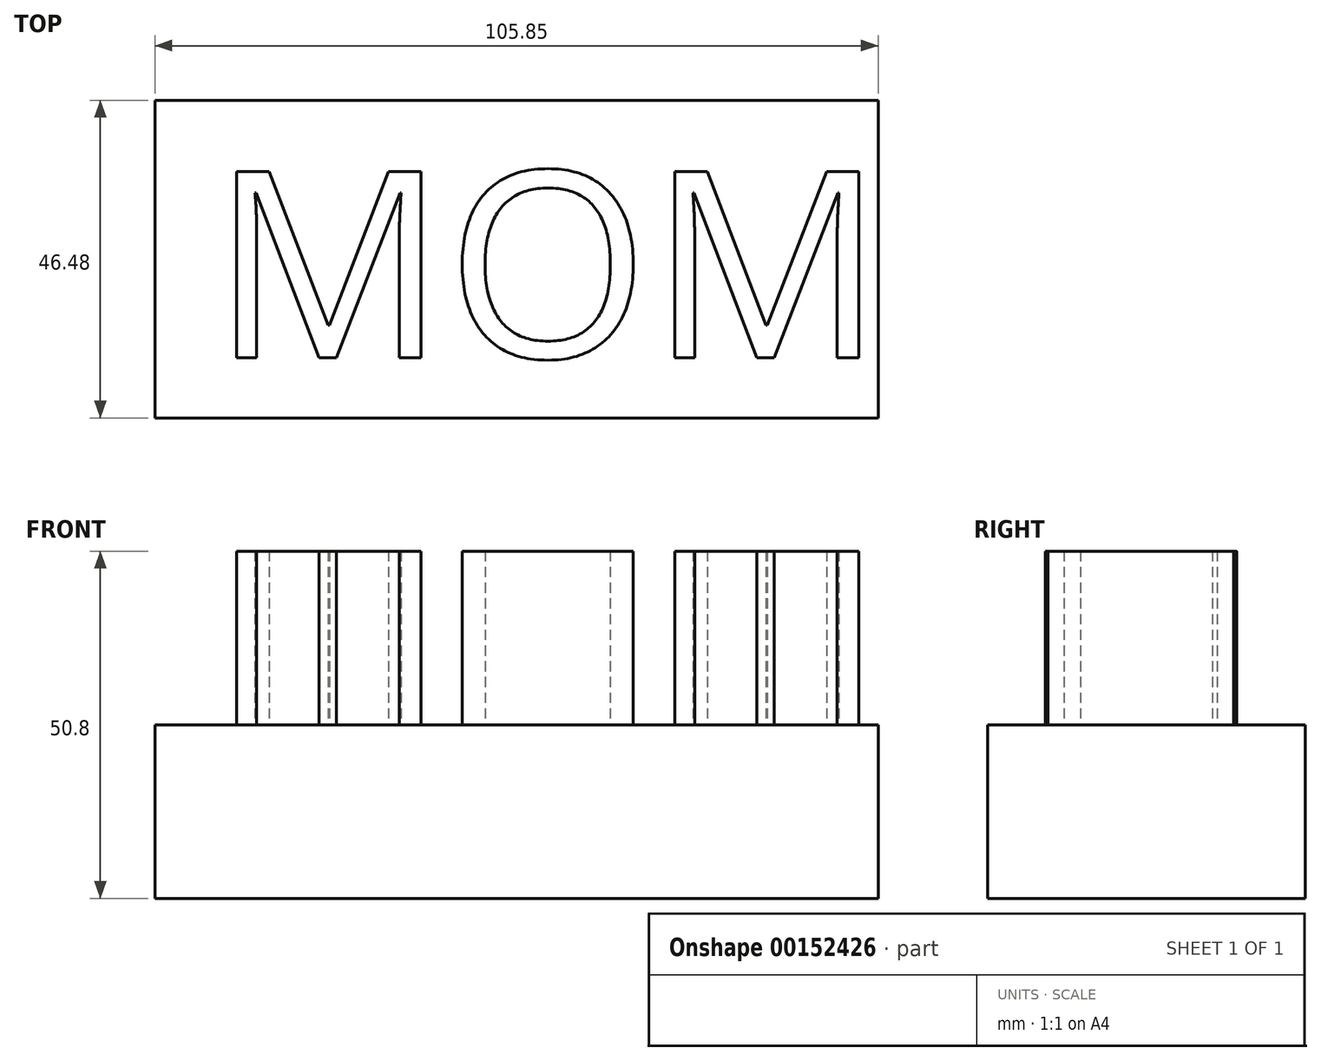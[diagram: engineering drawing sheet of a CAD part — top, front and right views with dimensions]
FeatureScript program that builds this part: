
annotation { "Feature Type Name" : "Feature", "Feature Type Description" : "" }
export const myFeature = defineFeature(function(context is Context, id is Id, definition is map)
    precondition{}
    {
        {
            var Q0;
            Q0=qCreatedBy(makeId("Top.planeOp"),FACE);
            var sketch = newSketch(context, id + "F0", { "sketchPlane" : qUnion([Q0])});
            skLineSegment(sketch, "E0.bottom", {"start": v(-45.3, 42.76) * mm, "end": v(35.16, 42.76) * mm});
            skLineSegment(sketch, "E0.top", {"start": v(-45.3, -3.72) * mm, "end": v(35.16, -3.72) * mm});
            skLineSegment(sketch, "E0.left", {"start": v(-45.3, 42.76) * mm, "end": v(-45.3, -3.72) * mm});
            skLineSegment(sketch, "E0.right", {"start": v(35.16, 42.76) * mm, "end": v(35.16, -3.72) * mm});
            skSolve(sketch);
        }
        {
            var Q0;
            Q0 = qSketchRegion(id + "F0", true);
            extrude(context, id + "F1", {"entities" : qUnion([Q0]), "depth" : 25.4 * mm});
        }
        {
            var Q0;
            Q0=makeQuery(id+"F1.opExtrude","CAP_FACE",FACE,{"disambiguationData":[OSD([sQuery(id+"F0.wireOp",EDGE,"E0.bottom"),sQuery(id+"F0.wireOp",EDGE,"E0.top"),sQuery(id+"F0.wireOp",EDGE,"E0.left"),sQuery(id+"F0.wireOp",EDGE,"E0.right")])],"isStart":false});
            var sketch = newSketch(context, id + "F2", { "sketchPlane" : qUnion([Q0])});
            skText(sketch, "E1", { "text": "MOM", "fontName": "OpenSans-Regular.ttf"});
            const initialGuessF2  = {"E1": [-0.03705, 0.0051, 1, 0, 0.02744]};
            skSetInitialGuess(sketch, initialGuessF2);
            skSolve(sketch);
        }
        {
            var Q0;
            Q0 = qSketchRegion(id + "F2", true);
            extrude(context, id + "F3", {"entities" : qUnion([Q0]), "operationType" : NewBodyOperationType.ADD, "depth" : 25.4 * mm});
        }
        {
            var Q0;
            Q0=makeQuery(id+"F1.opExtrude","SWEPT_FACE",FACE,{"disambiguationData":[OSD([sQuery(id+"F0.wireOp",EDGE,"E0.right")])]});
            var sketch = newSketch(context, id + "F4", { "sketchPlane" : qUnion([Q0])});
            skSolve(sketch);
        }
        {
            var Q0;
            Q0 = qSketchRegion(id + "F4", true);
            var Q1;
            {var subQ0=sQuery(id+"F0.wireOp",EDGE,"E0.right");Q1=makeQuery(id+"F4.imprint","IMPRINT",FACE,{"disambiguationData":[TD([[makeQuery(id+"F4.imprint","IMPRINT",EDGE,{"derivedFrom":makeQuery(id+"F1.opExtrude","CAP_EDGE",EDGE,{"disambiguationData":[OSD([subQ0])],"isStart":true})}),-1.0]])]});}
            extrude(context, id + "F5", {"entities" : qUnion([Q0, Q1]), "operationType" : NewBodyOperationType.ADD, "depth" : 25.4 * mm});
        }
    });
